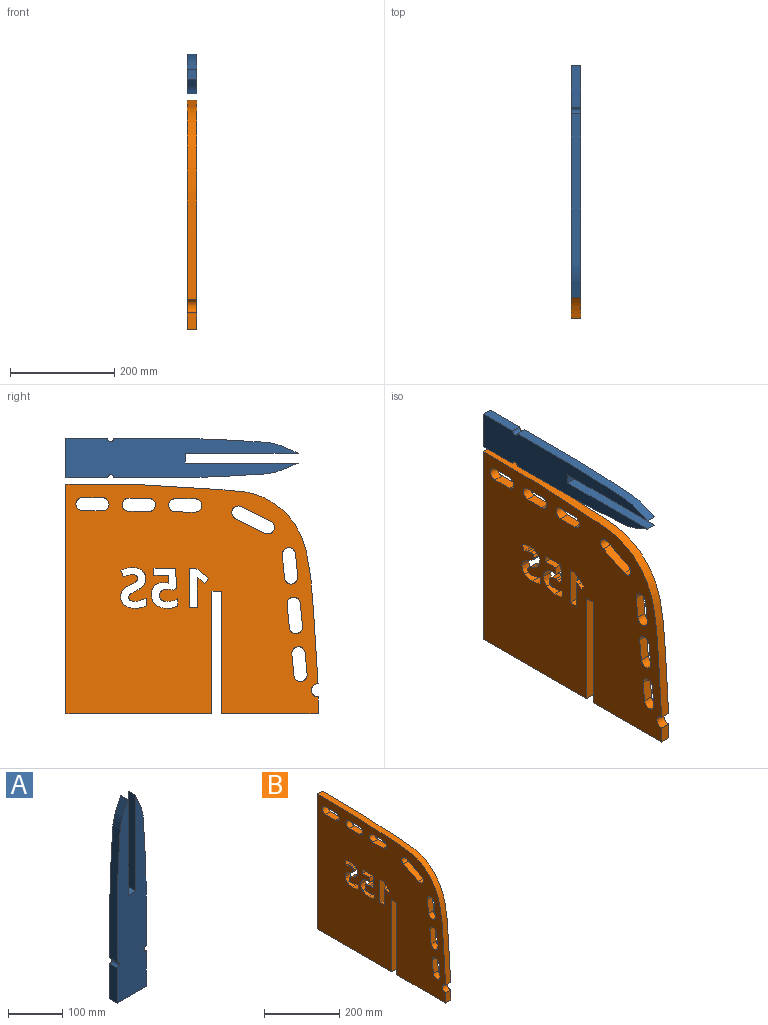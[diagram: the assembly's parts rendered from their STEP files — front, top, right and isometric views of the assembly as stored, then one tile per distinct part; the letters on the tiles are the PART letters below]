
ASSEMBLY  parts=2 mates=1
PART A: 12 faces, bbox 76.9x19.1x446.7 mm
  f0: extruded ~352.53x28.68mm, area 6781.9mm2, adj f1,f5,f6,f7
  f1: plane 216x19.05mm, normal (-1,0,0), area 4114.8mm2, adj f0,f2,f6,f7
  f2: plane 19.05x19.05mm, normal (0,0,1), area 362.9mm2, adj f1,f6,f7,f9
  f3: plane 76.2x19.05mm, normal (0,0,-1), area 1451.6mm2, adj f4,f6,f7,f10
  f4: plane 79.38x19.05mm, normal (1,0,0), area 1512.1mm2, adj f3,f5,f6,f7
  f5: cylinder r=6.35mm len=19.05mm, axis (0,1,0), area 380mm2, adj f0,f4,f6,f7
  f6: plane 446.7x76.92mm, normal (0,-1,0), area 26504.5mm2, adj f0,f1,f2,f3,f4,f5,f8,f9
  f7: plane 446.7x76.92mm, normal (0,1,0), area 26504.5mm2, adj f0,f1,f2,f3,f4,f5,f8,f9
  f8: extruded ~352.53x28.68mm, area 6781.9mm2, adj f6,f7,f9,f11
  f9: plane 216x19.05mm, normal (1,0,0), area 4114.8mm2, adj f2,f6,f7,f8
  f10: plane 79.38x19.05mm, normal (-1,0,0), area 1512.1mm2, adj f3,f6,f7,f11
  f11: cylinder r=6.35mm len=19.05mm, axis (0,1,0), area 380mm2, adj f6,f7,f8,f10
PART B: 97 faces, bbox 19.1x482.6x440.1 mm
  f0: plane 482.6x440.06mm, normal (1,0,0), area 177937.9mm2, adj f2,f3,f4,f5,f6,f7,f8,f9
  f1: plane 482.6x440.06mm, normal (-1,0,0), area 177937.9mm2, adj f2,f3,f4,f5,f6,f7,f8,f9
  f2: plane 41.23x19.05mm, normal (0,-1,0.1), area 789mm2, adj f0,f1,f37,f38
  f3: plane 41.23x19.05mm, normal (0,1,-0.1), area 789mm2, adj f0,f1,f37,f38
  f4: plane 32.43x19.05mm, normal (0,-1,0), area 617.7mm2, adj f0,f1,f5,f20
  f5: plane 184.15x19.05mm, normal (0,0,-1), area 3508.1mm2, adj f0,f1,f4,f6
  f6: plane 234.95x19.05mm, normal (0,1,0), area 4475.8mm2, adj f0,f1,f5,f7
  f7: plane 19.05x19.05mm, normal (0,0,-1), area 362.9mm2, adj f0,f1,f6,f8
  f8: plane 234.95x19.05mm, normal (0,-1,0), area 4475.8mm2, adj f0,f1,f7,f9
  f9: plane 279.4x19.05mm, normal (0,0,-1), area 5322.6mm2, adj f0,f1,f8,f10
  f10: plane 440.06x19.05mm, normal (0,1,0), area 8383mm2, adj f0,f1,f9,f11
  f11: extruded ~482.6x382.23mm, area 14692.3mm2, adj f0,f1,f10,f20
  f12: plane 38.1x19.05mm, normal (0,-0.01,1), area 725.9mm2, adj f0,f1,f35,f36
  f13: plane 38.1x19.05mm, normal (0,-0.01,1), area 725.9mm2, adj f0,f1,f33,f34
  f14: plane 38.1x19.05mm, normal (0,-0.01,1), area 725.9mm2, adj f0,f1,f31,f32
  f15: plane 56.27x28.13mm, normal (0,-0.45,0.89), area 1198.4mm2, adj f0,f1,f29,f30
  f16: plane 44.25x19.05mm, normal (0,1,-0.1), area 846.8mm2, adj f0,f1,f27,f28
  f17: plane 44.25x19.05mm, normal (0,-1,0.1), area 846.8mm2, adj f0,f1,f27,f28
  f18: plane 44.25x19.05mm, normal (0,1,-0.1), area 846.8mm2, adj f0,f1,f25,f26
  f19: plane 44.25x19.05mm, normal (0,-1,0.1), area 846.8mm2, adj f0,f1,f25,f26
  f20: cylinder r=12.7mm len=25.4mm, axis (-1,0,0), area 760.1mm2, adj f0,f1,f4,f11
  f21: plane 38.1x19.05mm, normal (0,0.01,-1), area 725.9mm2, adj f0,f1,f35,f36
  f22: plane 38.1x19.05mm, normal (0,0.01,-1), area 725.9mm2, adj f0,f1,f33,f34
  f23: plane 38.1x19.05mm, normal (0,0.01,-1), area 725.9mm2, adj f0,f1,f31,f32
  f24: plane 56.27x28.13mm, normal (0,0.45,-0.89), area 1198.4mm2, adj f0,f1,f29,f30
  f25: cylinder r=12.7mm len=25.34mm, axis (1,0,0), area 760.1mm2, adj f0,f1,f18,f19
  f26: cylinder r=12.7mm len=25.34mm, axis (1,0,0), area 760.1mm2, adj f0,f1,f18,f19
  f27: cylinder r=12.7mm len=25.34mm, axis (1,0,0), area 760.1mm2, adj f0,f1,f16,f17
  f28: cylinder r=12.7mm len=25.34mm, axis (1,0,0), area 760.1mm2, adj f0,f1,f16,f17
  f29: cylinder r=12.7mm len=24.06mm, axis (1,0,0), area 760.1mm2, adj f0,f1,f15,f24
  f30: cylinder r=12.7mm len=24.06mm, axis (1,0,0), area 760.1mm2, adj f0,f1,f15,f24
  f31: cylinder r=12.7mm len=25.4mm, axis (1,0,0), area 760.1mm2, adj f0,f1,f14,f23
  f32: cylinder r=12.7mm len=25.4mm, axis (1,0,0), area 760.1mm2, adj f0,f1,f14,f23
  f33: cylinder r=12.7mm len=25.4mm, axis (1,0,0), area 760.1mm2, adj f0,f1,f13,f22
  f34: cylinder r=12.7mm len=25.4mm, axis (1,0,0), area 760.1mm2, adj f0,f1,f13,f22
  f35: cylinder r=12.7mm len=25.4mm, axis (1,0,0), area 760.1mm2, adj f0,f1,f12,f21
  f36: cylinder r=12.7mm len=25.4mm, axis (1,0,0), area 760.1mm2, adj f0,f1,f12,f21
  f37: cylinder r=12.7mm len=25.34mm, axis (1,0,0), area 760.1mm2, adj f0,f1,f2,f3
  f38: cylinder r=12.7mm len=25.34mm, axis (1,0,0), area 760.1mm2, adj f0,f1,f2,f3
  f39: extruded ~19.05x12.48mm, area 253.9mm2, adj f0,f1,f40,f66
  f40: extruded ~19.05x14.53mm, area 340.5mm2, adj f0,f1,f39,f41
  f41: extruded ~19.05x10.15mm, area 218.1mm2, adj f0,f1,f40,f42
  f42: extruded ~19.05x3.13mm, area 83.8mm2, adj f0,f1,f41,f43
  f43: extruded ~19.05x3.7mm, area 73.8mm2, adj f0,f1,f42,f44
  f44: extruded ~19.05x5.52mm, area 118.8mm2, adj f0,f1,f43,f45
  f45: extruded ~19.05x6.98mm, area 142mm2, adj f0,f1,f44,f46
  f46: extruded ~19.05x7.77mm, area 149.6mm2, adj f0,f1,f45,f47
  f47: extruded ~19.05x10mm, area 201.9mm2, adj f0,f1,f46,f48
  f48: plane 19.05x12.47mm, normal (0,-0.92,0.38), area 257.1mm2, adj f0,f1,f47,f49
  f49: extruded ~19.05x11.19mm, area 226mm2, adj f0,f1,f48,f50
  f50: extruded ~19.05x11.24mm, area 216.3mm2, adj f0,f1,f49,f51
  f51: extruded ~19.05x18.79mm, area 382mm2, adj f0,f1,f50,f52
  f52: extruded ~19.05x15.77mm, area 338.4mm2, adj f0,f1,f51,f53
  f53: extruded ~19.05x9.29mm, area 183.1mm2, adj f0,f1,f52,f54
  f54: extruded ~19.05x6.98mm, area 170.7mm2, adj f0,f1,f53,f55
  f55: extruded ~19.05x10.38mm, area 231.4mm2, adj f0,f1,f54,f56
  f56: extruded ~19.05x9.8mm, area 210.7mm2, adj f0,f1,f55,f57
  f57: extruded ~19.05x3.65mm, area 94.6mm2, adj f0,f1,f56,f58
  f58: extruded ~19.05x3.95mm, area 80.2mm2, adj f0,f1,f57,f59
  f59: extruded ~19.05x5.99mm, area 131.5mm2, adj f0,f1,f58,f60
  f60: extruded ~19.05x8.08mm, area 161.1mm2, adj f0,f1,f59,f61
  f61: extruded ~19.05x9.7mm, area 187.2mm2, adj f0,f1,f60,f62
  f62: extruded ~19.05x12.94mm, area 263.3mm2, adj f0,f1,f61,f63
  f63: plane 19.05x14.88mm, normal (0,1,0), area 283.5mm2, adj f0,f1,f62,f64
  f64: extruded ~21.4x19.05mm, area 420.5mm2, adj f0,f1,f63,f65
  f65: extruded ~20.48x19.05mm, area 413.8mm2, adj f0,f1,f64,f66
  f66: extruded ~19.05x16.13mm, area 350.4mm2, adj f0,f1,f39,f65
  f67: extruded ~19.05x7.81mm, area 149.6mm2, adj f0,f1,f68,f86
  f68: plane 19.05x1.8mm, normal (0,0.2,-0.98), area 35mm2, adj f0,f1,f67,f69
  f69: plane 19.05x14.83mm, normal (0,-1,0.09), area 283.8mm2, adj f0,f1,f68,f70
  f70: plane 26.97x19.05mm, normal (0,0,1), area 513.8mm2, adj f0,f1,f69,f71
  f71: plane 19.05x13.54mm, normal (0,-1,0), area 258mm2, adj f0,f1,f70,f72
  f72: plane 40.98x19.05mm, normal (0,0,-1), area 780.6mm2, adj f0,f1,f71,f73
  f73: plane 38.5x19.05mm, normal (0,1,-0.07), area 735.4mm2, adj f0,f1,f72,f74
  f74: plane 19.05x6.37mm, normal (0,0.47,0.88), area 137.7mm2, adj f0,f1,f73,f75
  f75: extruded ~19.05x5.37mm, area 104.9mm2, adj f0,f1,f74,f76
  f76: extruded ~19.05x6.04mm, area 115.6mm2, adj f0,f1,f75,f77
  f77: extruded ~19.05x15.15mm, area 412.5mm2, adj f0,f1,f76,f78
  f78: extruded ~19.05x14.63mm, area 412.4mm2, adj f0,f1,f77,f79
  f79: extruded ~19.05x10.28mm, area 198mm2, adj f0,f1,f78,f80
  f80: extruded ~19.05x9.5mm, area 193.6mm2, adj f0,f1,f79,f81
  f81: plane 19.05x13.81mm, normal (0,1,0), area 263mm2, adj f0,f1,f80,f82
  f82: extruded ~20.36x19.05mm, area 399.3mm2, adj f0,f1,f81,f83
  f83: extruded ~22.32x19.05mm, area 454.5mm2, adj f0,f1,f82,f84
  f84: extruded ~19.48x19.05mm, area 412.9mm2, adj f0,f1,f83,f85
  f85: extruded ~19.05x16.85mm, area 354.2mm2, adj f0,f1,f84,f86
  f86: extruded ~19.05x17.44mm, area 361.2mm2, adj f0,f1,f67,f85
  f87: plane 75.56x19.05mm, normal (0,-1,0), area 1439.3mm2, adj f0,f1,f88,f96
  f88: plane 19.05x13.13mm, normal (0,0,-1), area 250.1mm2, adj f0,f1,f87,f89
  f89: plane 24.34x19.38mm, normal (0,0.62,-0.78), area 592.7mm2, adj f0,f1,f88,f90
  f90: plane 19.05x9.61mm, normal (0,0.78,0.63), area 234.6mm2, adj f0,f1,f89,f91
  f91: plane 19.05x8.68mm, normal (0,-0.63,0.78), area 212.2mm2, adj f0,f1,f90,f92
  f92: extruded ~19.05x5.52mm, area 144.7mm2, adj f0,f1,f91,f93
  f93: plane 19.05x7.86mm, normal (0,1,-0.03), area 149.7mm2, adj f0,f1,f92,f94
  f94: plane 19.05x7.18mm, normal (0,1,-0.02), area 136.8mm2, adj f0,f1,f93,f95
  f95: plane 43.72x19.05mm, normal (0,1,0), area 832.9mm2, adj f0,f1,f94,f96
  f96: plane 19.05x15.97mm, normal (0,0,1), area 304.3mm2, adj f0,f1,f87,f95
PLACE A rot(axis=(0.58,0.58,-0.58),120deg) t=(-183.23,237.66,471.72)mm
PLACE B t=(-192.75,-41.74,-17.97)mm
MATE planar A.f3 <-> B.f10  axis (0,1,0) through (-192.75,237.66,471.72)mm
